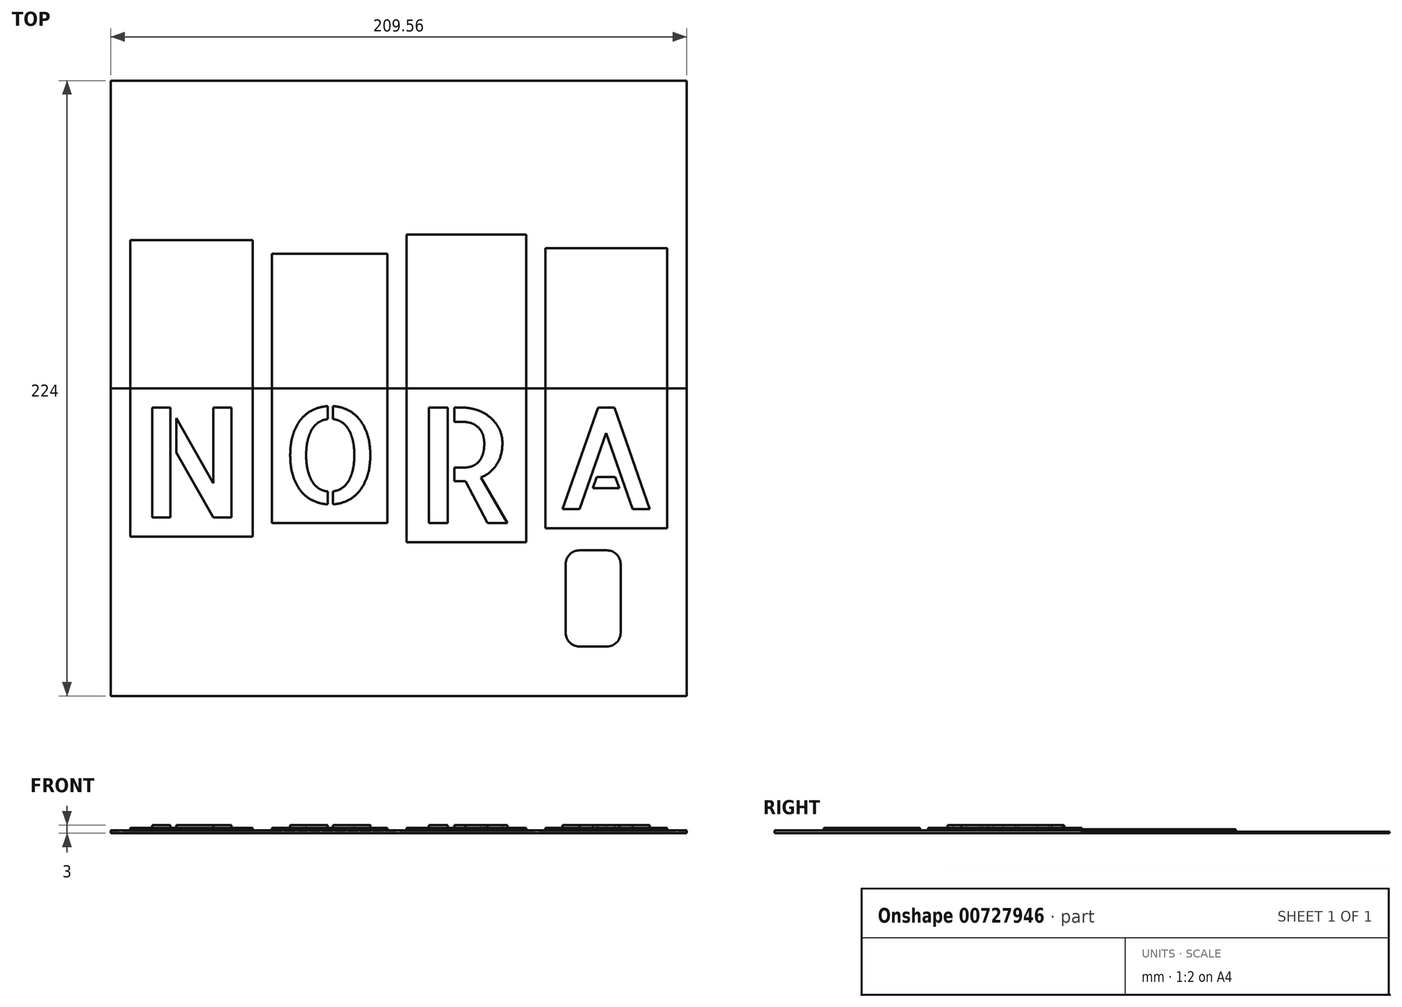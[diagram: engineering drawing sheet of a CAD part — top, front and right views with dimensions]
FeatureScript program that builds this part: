
annotation { "Feature Type Name" : "Feature", "Feature Type Description" : "" }
export const myFeature = defineFeature(function(context is Context, id is Id, definition is map)
    precondition{}
    {
        {
            var Q0;
            Q0=qCreatedBy(makeId("Top.planeOp"),FACE);
            var sketch = newSketch(context, id + "F0", { "sketchPlane" : qUnion([Q0])});
            skLineSegment(sketch, "E0.bottom", {"start": v(209.56, -112) * mm, "end": v(0, -112) * mm});
            skLineSegment(sketch, "E0.top", {"start": v(209.56, 112) * mm, "end": v(0, 112) * mm});
            skLineSegment(sketch, "E0.left", {"start": v(209.56, -112) * mm, "end": v(209.56, 112) * mm});
            skLineSegment(sketch, "E0.right", {"start": v(0, -112) * mm, "end": v(0, 112) * mm});
            skText(sketch, "E1", { "text": "N", "fontName": "AllertaStencil-Regular.ttf"});
            skText(sketch, "E2", { "text": "O", "fontName": "AllertaStencil-Regular.ttf"});
            skText(sketch, "E3", { "text": "R", "fontName": "AllertaStencil-Regular.ttf"});
            skText(sketch, "E4", { "text": "A", "fontName": "AllertaStencil-Regular.ttf"});
            skLineSegment(sketch, "E5", {"start": v(7, -54) * mm, "end": v(51.62, -54) * mm});
            skLineSegment(sketch, "E6", {"start": v(51.62, -54) * mm, "end": v(51.62, 0) * mm});
            skLineSegment(sketch, "E7", {"start": v(58.62, 0) * mm, "end": v(58.62, -49) * mm});
            skLineSegment(sketch, "E8", {"start": v(107.68, -56) * mm, "end": v(151.2, -56) * mm});
            skLineSegment(sketch, "E9", {"start": v(158.2, -51) * mm, "end": v(202.56, -51) * mm});
            skLineSegment(sketch, "E10", {"start": v(202.56, -51) * mm, "end": v(202.56, 0) * mm});
            skLineSegment(sketch, "E11", {"start": v(158.2, 0) * mm, "end": v(158.2, -51) * mm});
            skLineSegment(sketch, "E12", {"start": v(58.62, -49) * mm, "end": v(100.68, -49) * mm});
            skLineSegment(sketch, "E13", {"start": v(100.68, 0) * mm, "end": v(100.68, -49) * mm});
            skLineSegment(sketch, "E14", {"start": v(107.68, -56) * mm, "end": v(107.68, 0) * mm});
            skLineSegment(sketch, "E15", {"start": v(151.2, -56) * mm, "end": v(151.2, 0) * mm});
            skLineSegment(sketch, "E16", {"start": v(7, -54) * mm, "end": v(7, 0) * mm});
            skLineSegment(sketch, "E17", {"start": v(0, 0) * mm, "end": v(209.56, 0) * mm});
            skLineSegment(sketch, "E18.MirrorCS", {"start": v(202.56, 51) * mm, "end": v(202.56, 0) * mm});
            skLineSegment(sketch, "E19.MirrorCS", {"start": v(158.2, 51) * mm, "end": v(202.56, 51) * mm});
            skLineSegment(sketch, "E20.MirrorCS", {"start": v(158.2, 0) * mm, "end": v(158.2, 51) * mm});
            skLineSegment(sketch, "E21.MirrorCS", {"start": v(151.2, 56) * mm, "end": v(151.2, 0) * mm});
            skLineSegment(sketch, "E22.MirrorCS", {"start": v(107.68, 56) * mm, "end": v(151.2, 56) * mm});
            skLineSegment(sketch, "E23.MirrorCS", {"start": v(107.68, 56) * mm, "end": v(107.68, 0) * mm});
            skLineSegment(sketch, "E24.MirrorCS", {"start": v(100.68, 0) * mm, "end": v(100.68, 49) * mm});
            skLineSegment(sketch, "E25.MirrorCS", {"start": v(58.62, 49) * mm, "end": v(100.68, 49) * mm});
            skLineSegment(sketch, "E26.MirrorCS", {"start": v(58.62, 0) * mm, "end": v(58.62, 49) * mm});
            skLineSegment(sketch, "E27.MirrorCS", {"start": v(51.62, 54) * mm, "end": v(51.62, 0) * mm});
            skLineSegment(sketch, "E28.MirrorCS", {"start": v(7, 54) * mm, "end": v(7, 0) * mm});
            skLineSegment(sketch, "E29.MirrorCS", {"start": v(7, 54) * mm, "end": v(51.62, 54) * mm});
            const initialGuessF0  = {"E1": [0.01, -0.047, 1, 0, 0.04], "E2": [0.06162, -0.042, 1, 0, 0.035], "E3": [0.11068, -0.049, 1, 0, 0.042], "E4": [0.1612, -0.044, 1, 0, 0.037]};
            skSetInitialGuess(sketch, initialGuessF0);
            skSolve(sketch);
        }
        {
            var Q0;
            Q0=makeQuery(id+"F0.imprint","IMPRINT",FACE,{"disambiguationData":[TD([[makeQuery(id+"F0.imprint","IMPRINT",EDGE,{"derivedFrom":sQuery(id+"F0.wireOp",EDGE,"E0.bottom")}),-1.0]])]});
            extrude(context, id + "F1", {"entities" : qUnion([Q0]), "depth" : 1 * mm, "offsetDistance" : 25 * mm});
        }
        {
            var Q0;
            Q0=makeQuery(id+"F0.imprint","IMPRINT",FACE,{"disambiguationData":[TD([[makeQuery(id+"F0.imprint","IMPRINT",EDGE,{"derivedFrom":sQuery(id+"F0.wireOp",EDGE,"E1.sketch_text.stroke-0")}),1.0]])]});
            var Q1;
            Q1=makeQuery(id+"F0.imprint","IMPRINT",FACE,{"disambiguationData":[TD([[makeQuery(id+"F0.imprint","IMPRINT",EDGE,{"derivedFrom":sQuery(id+"F0.wireOp",EDGE,"E2.sketch_text.stroke-0")}),1.0]])]});
            var Q2;
            Q2=makeQuery(id+"F0.imprint","IMPRINT",FACE,{"disambiguationData":[TD([[makeQuery(id+"F0.imprint","IMPRINT",EDGE,{"derivedFrom":sQuery(id+"F0.wireOp",EDGE,"E3.sketch_text.stroke-7")}),1.0]])]});
            var Q3;
            Q3=makeQuery(id+"F0.imprint","IMPRINT",FACE,{"disambiguationData":[TD([[makeQuery(id+"F0.imprint","IMPRINT",EDGE,{"derivedFrom":sQuery(id+"F0.wireOp",EDGE,"E4.sketch_text.stroke-0")}),1.0]])]});
            var Q4;
            {var subQ2=sQuery(id+"F0.wireOp",EDGE,"66c86559-6d77-4ce7-8347-9c63a2ec0ef39.MirrorCS");Q4=makeQuery(id+"F0.imprint","IMPRINT",FACE,{"disambiguationData":[TD([[makeQuery(id+"F0.imprint","IMPRINT",EDGE,{"derivedFrom":subQ2}),-1.0]])]});}
            var Q5;
            {var subQ2=sQuery(id+"F0.wireOp",EDGE,"66c86559-6d77-4ce7-8347-9c63a2ec0ef36.MirrorCS");Q5=makeQuery(id+"F0.imprint","IMPRINT",FACE,{"disambiguationData":[TD([[makeQuery(id+"F0.imprint","IMPRINT",EDGE,{"derivedFrom":subQ2}),-1.0]])]});}
            var Q6;
            {var subQ2=sQuery(id+"F0.wireOp",EDGE,"66c86559-6d77-4ce7-8347-9c63a2ec0ef33.MirrorCS");Q6=makeQuery(id+"F0.imprint","IMPRINT",FACE,{"disambiguationData":[TD([[makeQuery(id+"F0.imprint","IMPRINT",EDGE,{"derivedFrom":subQ2}),-1.0]])]});}
            var Q7;
            {var subQ0=sQuery(id+"F0.wireOp",EDGE,"66c86559-6d77-4ce7-8347-9c63a2ec0ef30.MirrorCS");Q7=makeQuery(id+"F0.imprint","IMPRINT",FACE,{"disambiguationData":[TD([[makeQuery(id+"F0.imprint","IMPRINT",EDGE,{"derivedFrom":subQ0}),-1.0]])]});}
            extrude(context, id + "F2", {"entities" : qUnion([Q0, Q1, Q2, Q3, Q4, Q5, Q6, Q7]), "operationType" : NewBodyOperationType.ADD, "depth" : 2 * mm, "offsetDistance" : 25 * mm});
        }
        {
            var Q0;
            Q0=makeQuery(id+"F0.imprint","IMPRINT",FACE,{"disambiguationData":[TD([[makeQuery(id+"F0.imprint","IMPRINT",EDGE,{"derivedFrom":sQuery(id+"F0.wireOp",EDGE,"E1.sketch_text.stroke-0")}),-1.0]])]});
            var Q1;
            Q1=makeQuery(id+"F0.imprint","IMPRINT",FACE,{"disambiguationData":[TD([[makeQuery(id+"F0.imprint","IMPRINT",EDGE,{"derivedFrom":sQuery(id+"F0.wireOp",EDGE,"E2.sketch_text.stroke-0")}),-1.0]])]});
            var Q2;
            Q2=makeQuery(id+"F0.imprint","IMPRINT",FACE,{"disambiguationData":[TD([[makeQuery(id+"F0.imprint","IMPRINT",EDGE,{"derivedFrom":sQuery(id+"F0.wireOp",EDGE,"E3.sketch_text.stroke-0")}),-1.0]])]});
            var Q3;
            Q3=makeQuery(id+"F0.imprint","IMPRINT",FACE,{"disambiguationData":[TD([[makeQuery(id+"F0.imprint","IMPRINT",EDGE,{"derivedFrom":sQuery(id+"F0.wireOp",EDGE,"E4.sketch_text.stroke-0")}),-1.0]])]});
            var Q4;
            Q4=makeQuery(id+"F0.imprint","IMPRINT",FACE,{"disambiguationData":[TD([[makeQuery(id+"F0.imprint","IMPRINT",EDGE,{"derivedFrom":sQuery(id+"F0.wireOp",EDGE,"E1.sketch_text.stroke-7")}),-1.0]])]});
            var Q5;
            Q5=makeQuery(id+"F0.imprint","IMPRINT",FACE,{"disambiguationData":[TD([[makeQuery(id+"F0.imprint","IMPRINT",EDGE,{"derivedFrom":sQuery(id+"F0.wireOp",EDGE,"E2.sketch_text.stroke-18")}),-1.0]])]});
            var Q6;
            Q6=makeQuery(id+"F0.imprint","IMPRINT",FACE,{"disambiguationData":[TD([[makeQuery(id+"F0.imprint","IMPRINT",EDGE,{"derivedFrom":sQuery(id+"F0.wireOp",EDGE,"E3.sketch_text.stroke-4")}),-1.0]])]});
            var Q7;
            Q7=makeQuery(id+"F0.imprint","IMPRINT",FACE,{"disambiguationData":[TD([[makeQuery(id+"F0.imprint","IMPRINT",EDGE,{"derivedFrom":sQuery(id+"F0.wireOp",EDGE,"E4.sketch_text.stroke-7")}),-1.0]])]});
            extrude(context, id + "F3", {"entities" : qUnion([Q0, Q1, Q2, Q3, Q4, Q5, Q6, Q7]), "operationType" : NewBodyOperationType.ADD, "depth" : 3 * mm, "offsetDistance" : 25 * mm});
        }
        {
            var Q0;
            Q0=makeQuery(id+"F0.imprint","IMPRINT",FACE,{"disambiguationData":[TD([[makeQuery(id+"F0.imprint","IMPRINT",EDGE,{"derivedFrom":sQuery(id+"F0.wireOp",EDGE,"E2.sketch_text.stroke-8")}),1.0]])]});
            var Q1;
            Q1=makeQuery(id+"F0.imprint","IMPRINT",FACE,{"disambiguationData":[TD([[makeQuery(id+"F0.imprint","IMPRINT",EDGE,{"derivedFrom":sQuery(id+"F0.wireOp",EDGE,"E3.sketch_text.stroke-0")}),1.0]])]});
            var Q2;
            Q2=makeQuery(id+"F0.imprint","IMPRINT",FACE,{"disambiguationData":[TD([[makeQuery(id+"F0.imprint","IMPRINT",EDGE,{"derivedFrom":sQuery(id+"F0.wireOp",EDGE,"E4.sketch_text.stroke-8")}),1.0]])]});
            extrude(context, id + "F4", {"entities" : qUnion([Q0, Q1, Q2]), "operationType" : NewBodyOperationType.ADD, "depth" : 2 * mm, "offsetDistance" : 25 * mm});
        }
        {
            var Q0;
            {var subQ8=sQuery(id+"F0.wireOp",EDGE,"E0.top");Q0=makeQuery(id+"F0.imprint","IMPRINT",FACE,{"disambiguationData":[TD([[makeQuery(id+"F0.imprint","IMPRINT",EDGE,{"derivedFrom":subQ8}),1.0]])]});}
            extrude(context, id + "F5", {"entities" : qUnion([Q0]), "operationType" : NewBodyOperationType.ADD, "depth" : 0.5 * mm, "offsetDistance" : 25 * mm});
        }
        {
            var Q0;
            {var subQ0=sQuery(id+"F0.wireOp",EDGE,"E27.MirrorCS");Q0=makeQuery(id+"F0.imprint","IMPRINT",FACE,{"disambiguationData":[TD([[makeQuery(id+"F0.imprint","IMPRINT",EDGE,{"derivedFrom":subQ0}),-1.0]])]});}
            var Q1;
            {var subQ2=sQuery(id+"F0.wireOp",EDGE,"E24.MirrorCS");Q1=makeQuery(id+"F0.imprint","IMPRINT",FACE,{"disambiguationData":[TD([[makeQuery(id+"F0.imprint","IMPRINT",EDGE,{"derivedFrom":subQ2}),1.0]])]});}
            var Q2;
            {var subQ2=sQuery(id+"F0.wireOp",EDGE,"E21.MirrorCS");Q2=makeQuery(id+"F0.imprint","IMPRINT",FACE,{"disambiguationData":[TD([[makeQuery(id+"F0.imprint","IMPRINT",EDGE,{"derivedFrom":subQ2}),-1.0]])]});}
            var Q3;
            {var subQ0=sQuery(id+"F0.wireOp",EDGE,"E18.MirrorCS");Q3=makeQuery(id+"F0.imprint","IMPRINT",FACE,{"disambiguationData":[TD([[makeQuery(id+"F0.imprint","IMPRINT",EDGE,{"derivedFrom":subQ0}),-1.0]])]});}
            extrude(context, id + "F6", {"entities" : qUnion([Q0, Q1, Q2, Q3]), "operationType" : NewBodyOperationType.ADD, "depth" : 1.5 * mm, "offsetDistance" : 25 * mm});
        }
        {
            var Q0;
            Q0=makeQuery(id+"F1.opExtrude","CAP_FACE",FACE,{"disambiguationData":[OSD([sQuery(id+"F0.wireOp",EDGE,"E0.bottom"),sQuery(id+"F0.wireOp",EDGE,"E0.left"),sQuery(id+"F0.wireOp",EDGE,"E0.right"),sQuery(id+"F0.wireOp",EDGE,"E5"),sQuery(id+"F0.wireOp",EDGE,"E6"),sQuery(id+"F0.wireOp",EDGE,"E7"),sQuery(id+"F0.wireOp",EDGE,"E8"),sQuery(id+"F0.wireOp",EDGE,"E9"),sQuery(id+"F0.wireOp",EDGE,"E10"),sQuery(id+"F0.wireOp",EDGE,"E11"),sQuery(id+"F0.wireOp",EDGE,"E12"),sQuery(id+"F0.wireOp",EDGE,"E13"),sQuery(id+"F0.wireOp",EDGE,"E14"),sQuery(id+"F0.wireOp",EDGE,"E15"),sQuery(id+"F0.wireOp",EDGE,"E16"),sQuery(id+"F0.wireOp",EDGE,"E17")])],"isStart":false});
            var sketch = newSketch(context, id + "F7", { "sketchPlane" : qUnion([Q0])});
            skLineSegment(sketch, "E30.bottom", {"start": v(170.56, -59) * mm, "end": v(180.56, -59) * mm});
            skLineSegment(sketch, "E30.top", {"start": v(170.56, -94) * mm, "end": v(180.56, -94) * mm});
            skLineSegment(sketch, "E30.left", {"start": v(165.56, -64) * mm, "end": v(165.56, -89) * mm});
            skLineSegment(sketch, "E30.right", {"start": v(185.56, -64) * mm, "end": v(185.56, -89) * mm});
            skPoint(sketch, "E31.visualSharp", {"position": v(165.56, -59) * mm});
            skArc(sketch, "E31.filletArc", {"start": v(170.56, -59) * mm, "mid": v(167.02, -60.46) * mm, "end": v(165.56, -64) * mm});
            skPoint(sketch, "E32.visualSharp", {"position": v(185.56, -59) * mm});
            skArc(sketch, "E32.filletArc", {"start": v(185.56, -64) * mm, "mid": v(184.1, -60.46) * mm, "end": v(180.56, -59) * mm});
            skPoint(sketch, "E33.visualSharp", {"position": v(185.56, -94) * mm});
            skArc(sketch, "E33.filletArc", {"start": v(180.56, -94) * mm, "mid": v(184.1, -92.54) * mm, "end": v(185.56, -89) * mm});
            skPoint(sketch, "E34.visualSharp", {"position": v(165.56, -94) * mm});
            skArc(sketch, "E34.filletArc", {"start": v(165.56, -89) * mm, "mid": v(167.02, -92.54) * mm, "end": v(170.56, -94) * mm});
            skSolve(sketch);
        }
        {
            var Q0;
            Q0=makeQuery(id+"F7.imprint","IMPRINT",FACE,{"disambiguationData":[TD([[makeQuery(id+"F7.imprint","IMPRINT",EDGE,{"derivedFrom":sQuery(id+"F7.wireOp",EDGE,"E30.bottom")}),-1.0]])]});
            extrude(context, id + "F8", {"entities" : qUnion([Q0]), "operationType" : NewBodyOperationType.ADD, "depth" : 1 * mm, "offsetDistance" : 25 * mm});
        }
    });
